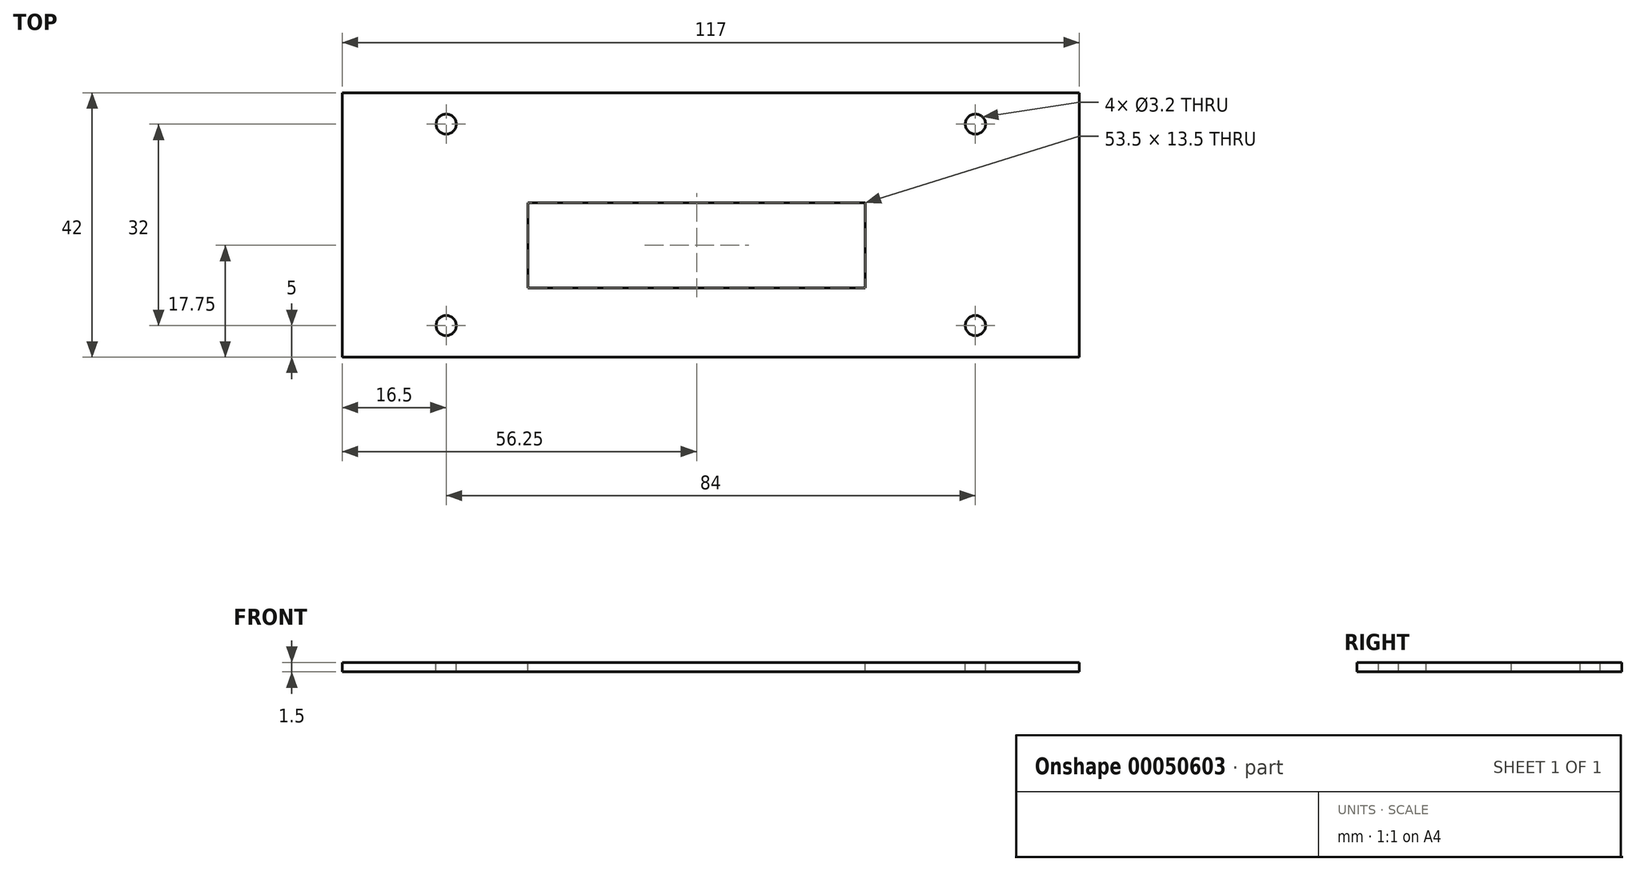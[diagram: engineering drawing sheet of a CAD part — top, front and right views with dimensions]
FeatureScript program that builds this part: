
annotation { "Feature Type Name" : "Feature", "Feature Type Description" : "" }
export const myFeature = defineFeature(function(context is Context, id is Id, definition is map)
    precondition{}
    {
        {
            var Q0;
            Q0=qCreatedBy(makeId("Top.planeOp"),FACE);
            var sketch = newSketch(context, id + "F0", { "sketchPlane" : qUnion([Q0])});
            skLineSegment(sketch, "E0.rect.bottom", {"start": v(58.5, 21) * mm, "end": v(-58.5, 21) * mm});
            skLineSegment(sketch, "E0.rect.top", {"start": v(58.5, -21) * mm, "end": v(-58.5, -21) * mm});
            skLineSegment(sketch, "E0.rect.left", {"start": v(58.5, 21) * mm, "end": v(58.5, -21) * mm});
            skLineSegment(sketch, "E0.rect.right", {"start": v(-58.5, 21) * mm, "end": v(-58.5, -21) * mm});
            skPoint(sketch, "E0.rect.middle", {"position": v(0, 0) * mm});
            skCircle(sketch, "E1", {"center": v(-42, 16) * mm, "radius": 1.6 * mm});
            skCircle(sketch, "E2", {"center": v(42, 16) * mm, "radius": 1.6 * mm});
            skCircle(sketch, "E3", {"center": v(42, -16) * mm, "radius": 1.6 * mm});
            skCircle(sketch, "E4", {"center": v(-42, -16) * mm, "radius": 1.6 * mm});
            skLineSegment(sketch, "E5.bottom", {"start": v(-29, 3.5) * mm, "end": v(24.5, 3.5) * mm});
            skLineSegment(sketch, "E5.top", {"start": v(-29, -10) * mm, "end": v(24.5, -10) * mm});
            skLineSegment(sketch, "E5.left", {"start": v(-29, 3.5) * mm, "end": v(-29, -10) * mm});
            skLineSegment(sketch, "E5.right", {"start": v(24.5, 3.5) * mm, "end": v(24.5, -10) * mm});
            skSolve(sketch);
        }
        {
            var Q0;
            Q0=makeQuery(id+"F0.imprint","IMPRINT",FACE,{"disambiguationData":[TD([[makeQuery(id+"F0.imprint","IMPRINT",EDGE,{"derivedFrom":sQuery(id+"F0.wireOp",EDGE,"E0.rect.bottom")}),1.0]])]});
            extrude(context, id + "F1", {"entities" : qUnion([Q0]), "oppositeDirection" : true, "depth" : 1.5 * mm});
        }
    });
